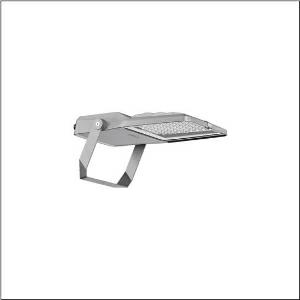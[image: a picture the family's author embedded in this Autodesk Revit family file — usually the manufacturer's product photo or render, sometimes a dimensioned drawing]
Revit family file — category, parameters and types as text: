
# Revit family: floodlight_fl_21_mini___pl52_5xa7776b4d1a_8ffb
name_source: partatom
category: Lighting Fixtures
units: mm (PartAtom-declared; Revit-internal decimal feet)

## family parameters
Cut with Voids When Loaded = No
Host = Face
Light Source = No
Part Type = Normal
Room Calculation Point = No
Round Connector Dimension = Use Diameter
Shared = No

## types (1)
- --- (1 x LED, 6480 lm, 45.7 W, 4000K)
    Apparent Load = 46 VA
    CIE Flux Codes = 26 60 98 100 100
    Color Rendering = 70
    Color Temperature = 4000K
    Default Elevation = 1800 mm
    Description = Floodlight FL 21 mini, floodlight, primary light control with lens, of PMMA, primary optical cover: protective disc, of toughened safety glass, transparent, light distribution: PL52, light emission: direct distribution, installation type: surface-mounted, LED, High Power LED, rated luminous flux: 6.480lm, luminous efficacy: 142lm/W, light colour: 740, colour temperature: 4000K, control gear: D4iSmart Interface (Zhaga), control: overheat protection, constant luminous flux control, time-dependent luminous flux control, flexible luminous flux parameterisation, pre-setting: logarithmic dimming characteristic, with terminal, 6-pole, mains connection: 220..240V, AC, 50/60Hz, start of lifetime: 46W, end of service life: 48W, reduction: 22W, mounting bracket, of diecast aluminium, powder-coated, Siteco® metallic grey (DB 702S), corrosivity category C5 mid according to DIN EN ISO 12944, suitable for swimming pools, chlorine-resistant, sealing non-destructively replaceable, mounting bracket, of steel, galvanised, powder-coated, Siteco® metallic grey (DB 702S), Smart Interface below and above, protection rating (complete): IP66, insulation class (complete): insulation class II (safety insulation), certification: CE, ENEC, VDE, protection symbol: D, impact resistance: IK08, permissible operating ambient temperature: -40..+40°C, permissible operating ambient temperature for outdoor applications: -40..+50°C, standard: DIN EN 12944, LABS conformity tested according to VDMA 24364:2018-05, packaging unit: 1 piece

Light Distribution: PL52
    Height = 70 mm
    Lamp = 1 x LED
    Lamp Light Flux = 6480 lm
    Lamp Power = 45.7 W
    Lamp count = 1
    Length = 485 mm
    Luminous efficacy = 142 lm/W
    Manufacturer = Siteco
    ModVariant = No
    Model = 5XA7776B4D1A
    Number of Poles = 1
    OnlyDefault = Yes
    Power Factor = 1
    Product Name = Floodlight FL 21 mini | PL52
    Product group = floodlight | pylon annexe
    ProductGroupID = 6200
    Protection Class = Protection class II
    Protection Degree = IP 66
    RLX_Detail_Level = 1
    RLX_Emergency_Light_Flux = 0 lm
    RLX_Emergency_Type = 0
    RLX_Emergency_Type_DB = No
    RlxData = <blob elided: 96337 chars, md5=2bdcd1fa>
    Socket = socket
    Standby Power = 0 W
    System Light Flux = 6480 lm
    System Power = 46 W
    Type Comments = factory setting: luminous flux: 100 % | dim-lin: 254 | 463 mA
    Type Image = l_1006845.jpg
    URL = http://relux.com
    VarID = @adj_095474
    Voltage = 0 V
    Weight = 0.00 kg
    Width = 337 mm

## geometry (parser evidence)
native form markers: Blend x4, Sweep x10
no freeform markers — native parametric forms only
